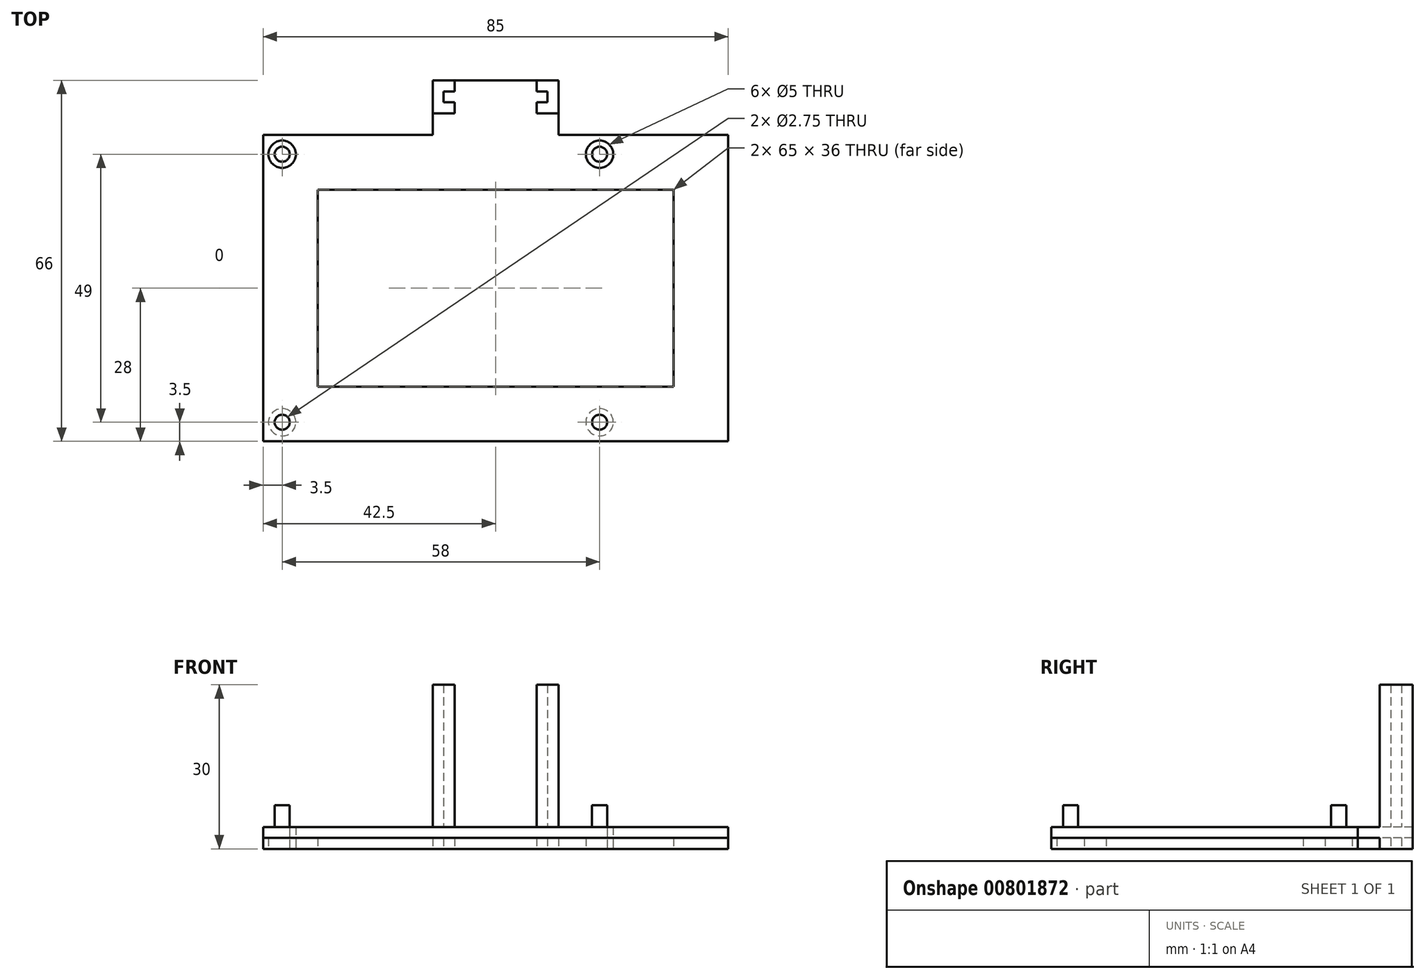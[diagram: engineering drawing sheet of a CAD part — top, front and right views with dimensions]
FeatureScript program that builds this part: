
annotation { "Feature Type Name" : "Feature", "Feature Type Description" : "" }
export const myFeature = defineFeature(function(context is Context, id is Id, definition is map)
    precondition{}
    {
        {
            var Q0;
            Q0=qCreatedBy(makeId("Top.planeOp"),FACE);
            var sketch = newSketch(context, id + "F0", { "sketchPlane" : qUnion([Q0])});
            skLineSegment(sketch, "E0", {"start": v(0, 0) * mm, "end": v(3.5, 0) * mm, "construction": true});
            skLineSegment(sketch, "E1", {"start": v(3.5, 0) * mm, "end": v(3.5, 3.5) * mm, "construction": true});
            skLineSegment(sketch, "E2.bottom", {"start": v(0, 0) * mm, "end": v(85, 0) * mm});
            skLineSegment(sketch, "E3", {"start": v(3.5, 3.5) * mm, "end": v(61.5, 3.5) * mm, "construction": true});
            skLineSegment(sketch, "E4", {"start": v(85, 0) * mm, "end": v(85, 28) * mm});
            skLineSegment(sketch, "E5", {"start": v(0, 0) * mm, "end": v(0, 28) * mm});
            skCircle(sketch, "E6", {"center": v(3.5, 3.5) * mm, "radius": 2.5 * mm});
            skCircle(sketch, "E7", {"center": v(61.5, 3.5) * mm, "radius": 2.5 * mm});
            skLineSegment(sketch, "E8", {"start": v(0, 28) * mm, "end": v(85, 28) * mm, "construction": true});
            skCircle(sketch, "E9.MirrorC", {"center": v(61.5, 52.5) * mm, "radius": 2.5 * mm});
            skLineSegment(sketch, "E10.MirrorCS", {"start": v(3.5, 52.5) * mm, "end": v(61.5, 52.5) * mm, "construction": true});
            skLineSegment(sketch, "E11.MirrorCS", {"start": v(3.5, 56) * mm, "end": v(3.5, 52.5) * mm, "construction": true});
            skLineSegment(sketch, "E12.MirrorCS", {"start": v(85, 56) * mm, "end": v(85, 28) * mm});
            skCircle(sketch, "E13.MirrorC", {"center": v(3.5, 52.5) * mm, "radius": 2.5 * mm});
            skLineSegment(sketch, "E14.MirrorCS", {"start": v(0, 56) * mm, "end": v(0, 28) * mm});
            skLineSegment(sketch, "E15.MirrorCS", {"start": v(0, 56) * mm, "end": v(3.5, 56) * mm, "construction": true});
            skLineSegment(sketch, "E16", {"start": v(0, 56) * mm, "end": v(10, 56) * mm, "construction": true});
            skLineSegment(sketch, "E17", {"start": v(10, 56) * mm, "end": v(10, 46) * mm, "construction": true});
            skLineSegment(sketch, "E18", {"start": v(85, 0) * mm, "end": v(75, 0) * mm, "construction": true});
            skLineSegment(sketch, "E19", {"start": v(75, 0) * mm, "end": v(75, 10) * mm, "construction": true});
            skLineSegment(sketch, "E20.bottom", {"start": v(10, 46) * mm, "end": v(75, 46) * mm});
            skLineSegment(sketch, "E20.top", {"start": v(10, 10) * mm, "end": v(75, 10) * mm});
            skLineSegment(sketch, "E20.left", {"start": v(10, 46) * mm, "end": v(10, 10) * mm});
            skLineSegment(sketch, "E20.right", {"start": v(75, 46) * mm, "end": v(75, 10) * mm});
            skLineSegment(sketch, "E21", {"start": v(42.5, 56) * mm, "end": v(54, 56) * mm, "construction": true});
            skLineSegment(sketch, "E22", {"start": v(54, 56) * mm, "end": v(54, 66) * mm});
            skLineSegment(sketch, "E23", {"start": v(54, 66) * mm, "end": v(50, 66) * mm});
            skLineSegment(sketch, "E24", {"start": v(50, 66) * mm, "end": v(50, 64) * mm});
            skLineSegment(sketch, "E25", {"start": v(50, 64) * mm, "end": v(52, 64) * mm});
            skLineSegment(sketch, "E26", {"start": v(52, 64) * mm, "end": v(52, 62) * mm});
            skLineSegment(sketch, "E27", {"start": v(52, 62) * mm, "end": v(50, 62) * mm});
            skLineSegment(sketch, "E28", {"start": v(42.5, 56) * mm, "end": v(42.5, 66) * mm, "construction": true});
            skLineSegment(sketch, "E29.MirrorCS", {"start": v(35, 64) * mm, "end": v(33, 64) * mm});
            skLineSegment(sketch, "E30.MirrorCS", {"start": v(35, 66) * mm, "end": v(35, 64) * mm});
            skLineSegment(sketch, "E31.MirrorCS", {"start": v(33, 64) * mm, "end": v(33, 62) * mm});
            skLineSegment(sketch, "E32.MirrorCS", {"start": v(33, 62) * mm, "end": v(35, 62) * mm});
            skLineSegment(sketch, "E33.MirrorCS", {"start": v(31, 66) * mm, "end": v(35, 66) * mm});
            skLineSegment(sketch, "E34", {"start": v(31, 66) * mm, "end": v(31, 56) * mm});
            skLineSegment(sketch, "E35", {"start": v(35, 66) * mm, "end": v(50, 66) * mm});
            skCircle(sketch, "E36", {"center": v(3.5, 52.5) * mm, "radius": 1.38 * mm});
            skCircle(sketch, "E37", {"center": v(61.5, 52.5) * mm, "radius": 1.38 * mm});
            skCircle(sketch, "E38", {"center": v(61.5, 3.5) * mm, "radius": 1.38 * mm});
            skCircle(sketch, "E39", {"center": v(3.5, 3.5) * mm, "radius": 1.38 * mm});
            skLineSegment(sketch, "E40", {"start": v(35, 62) * mm, "end": v(35, 60) * mm});
            skLineSegment(sketch, "E41", {"start": v(50, 62) * mm, "end": v(50, 60) * mm});
            skLineSegment(sketch, "E42", {"start": v(35, 60) * mm, "end": v(31, 60) * mm});
            skPoint(sketch, "E42.endSnap0", {"position": v(31, 61) * mm});
            skLineSegment(sketch, "E43", {"start": v(50, 60) * mm, "end": v(54, 60) * mm});
            skLineSegment(sketch, "E44", {"start": v(0, 56) * mm, "end": v(31, 56) * mm});
            skLineSegment(sketch, "E45", {"start": v(54, 56) * mm, "end": v(85, 56) * mm});
            skSolve(sketch);
        }
        {
            var Q0;
            Q0=makeQuery(id+"F0.imprint","IMPRINT",FACE,{"disambiguationData":[TD([[makeQuery(id+"F0.imprint","IMPRINT",EDGE,{"derivedFrom":sQuery(id+"F0.wireOp",EDGE,"E29.MirrorCS")}),-1.0]])]});
            var Q1;
            {var subQ0=sQuery(id+"F0.wireOp",EDGE,"E22");Q1=makeQuery(id+"F0.imprint","IMPRINT",FACE,{"disambiguationData":[TD([[makeQuery(id+"F0.imprint","IMPRINT",EDGE,{"derivedFrom":subQ0}),1.0]])]});}
            extrude(context, id + "F1", {"entities" : qUnion([Q0, Q1]), "depth" : 30 * mm, "offsetDistance" : 25 * mm});
        }
        {
            var Q0;
            Q0=makeQuery(id+"F0.imprint","IMPRINT",FACE,{"disambiguationData":[TD([[makeQuery(id+"F0.imprint","IMPRINT",EDGE,{"derivedFrom":sQuery(id+"F0.wireOp",EDGE,"E13.MirrorC")}),-1.0]])]});
            var Q1;
            Q1=makeQuery(id+"F0.imprint","IMPRINT",FACE,{"disambiguationData":[TD([[makeQuery(id+"F0.imprint","IMPRINT",EDGE,{"derivedFrom":sQuery(id+"F0.wireOp",EDGE,"E9.MirrorC")}),-1.0]])]});
            var Q2;
            Q2=makeQuery(id+"F0.imprint","IMPRINT",FACE,{"disambiguationData":[TD([[makeQuery(id+"F0.imprint","IMPRINT",EDGE,{"derivedFrom":sQuery(id+"F0.wireOp",EDGE,"E7")}),1.0]])]});
            var Q3;
            Q3=makeQuery(id+"F0.imprint","IMPRINT",FACE,{"disambiguationData":[TD([[makeQuery(id+"F0.imprint","IMPRINT",EDGE,{"derivedFrom":sQuery(id+"F0.wireOp",EDGE,"E6")}),1.0]])]});
            extrude(context, id + "F2", {"entities" : qUnion([Q0, Q1, Q2, Q3]), "operationType" : NewBodyOperationType.ADD, "depth" : 4 * mm, "offsetDistance" : 25 * mm});
        }
        {
            var Q0;
            Q0=makeQuery(id+"F0.imprint","IMPRINT",FACE,{"disambiguationData":[TD([[makeQuery(id+"F0.imprint","IMPRINT",EDGE,{"derivedFrom":sQuery(id+"F0.wireOp",EDGE,"E36")}),1.0]])]});
            var Q1;
            Q1=makeQuery(id+"F0.imprint","IMPRINT",FACE,{"disambiguationData":[TD([[makeQuery(id+"F0.imprint","IMPRINT",EDGE,{"derivedFrom":sQuery(id+"F0.wireOp",EDGE,"E37")}),1.0]])]});
            var Q2;
            Q2=makeQuery(id+"F0.imprint","IMPRINT",FACE,{"disambiguationData":[TD([[makeQuery(id+"F0.imprint","IMPRINT",EDGE,{"derivedFrom":sQuery(id+"F0.wireOp",EDGE,"E38")}),1.0]])]});
            var Q3;
            Q3=makeQuery(id+"F0.imprint","IMPRINT",FACE,{"disambiguationData":[TD([[makeQuery(id+"F0.imprint","IMPRINT",EDGE,{"derivedFrom":sQuery(id+"F0.wireOp",EDGE,"E39")}),1.0]])]});
            extrude(context, id + "F3", {"entities" : qUnion([Q0, Q1, Q2, Q3]), "depth" : 8 * mm, "offsetDistance" : 25 * mm});
        }
        {
            var Q0;
            Q0=makeQuery(id+"F0.imprint","IMPRINT",FACE,{"disambiguationData":[TD([[makeQuery(id+"F0.imprint","IMPRINT",EDGE,{"derivedFrom":sQuery(id+"F0.wireOp",EDGE,"E2.bottom")}),1.0]])]});
            extrude(context, id + "F4", {"entities" : qUnion([Q0]), "depth" : 2 * mm, "offsetDistance" : 25 * mm});
        }
    });
